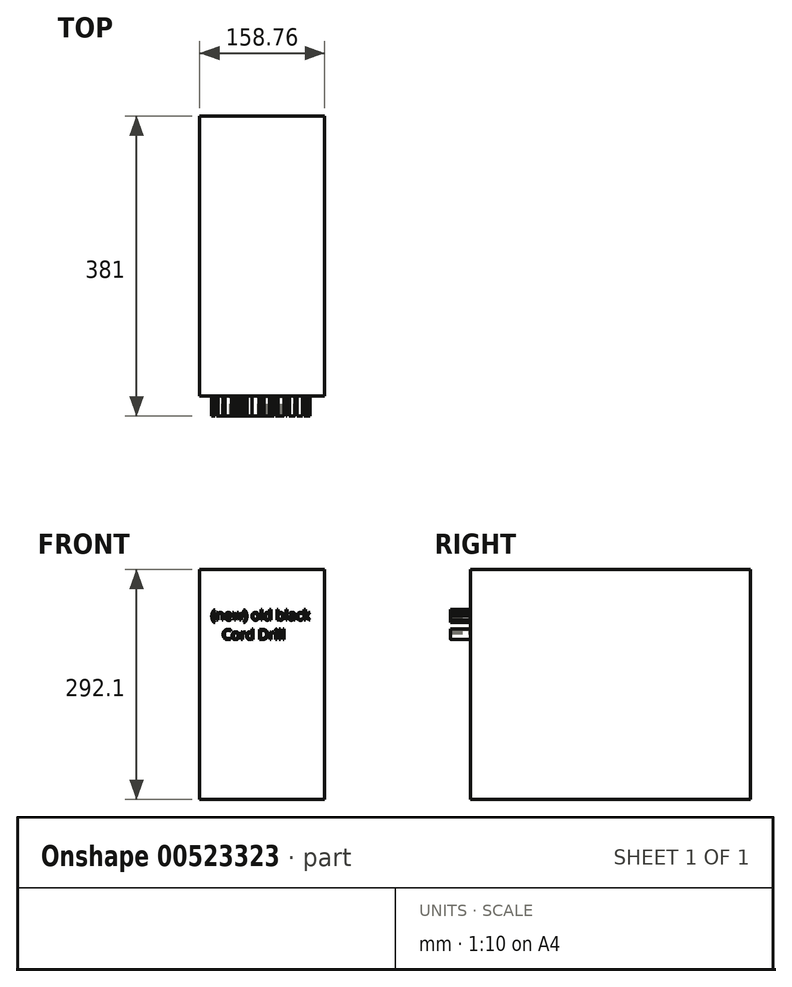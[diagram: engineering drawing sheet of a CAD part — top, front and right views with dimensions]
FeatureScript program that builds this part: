
annotation { "Feature Type Name" : "Feature", "Feature Type Description" : "" }
export const myFeature = defineFeature(function(context is Context, id is Id, definition is map)
    precondition{}
    {
        {
            var Q0;
            Q0=qCreatedBy(makeId("Front.planeOp"),FACE);
            var sketch = newSketch(context, id + "F0", { "sketchPlane" : qUnion([Q0])});
            skLineSegment(sketch, "E0.bottom", {"start": v(79.37, 146.05) * mm, "end": v(-79.38, 146.05) * mm});
            skLineSegment(sketch, "E0.top", {"start": v(79.38, -146.05) * mm, "end": v(-79.37, -146.05) * mm});
            skLineSegment(sketch, "E0.left", {"start": v(79.37, 146.05) * mm, "end": v(79.38, -146.05) * mm});
            skLineSegment(sketch, "E0.right", {"start": v(-79.38, 146.05) * mm, "end": v(-79.37, -146.05) * mm});
            skPoint(sketch, "E0.middle", {"position": v(0, 0) * mm});
            skSolve(sketch);
        }
        {
            var Q0;
            Q0=makeQuery(id+"F0.imprint","IMPRINT",FACE,{"disambiguationData":[TD([[makeQuery(id+"F0.imprint","IMPRINT",EDGE,{"derivedFrom":sQuery(id+"F0.wireOp",EDGE,"E0.bottom")}),1.0]])]});
            extrude(context, id + "F1", {"entities" : qUnion([Q0]), "depth" : 355.6 * mm, "offsetDistance" : 25.4 * mm});
        }
        {
            var Q0;
            Q0=makeQuery(id+"F1.opExtrude","CAP_FACE",FACE,{"disambiguationData":[OSD([sQuery(id+"F0.wireOp",EDGE,"E0.bottom"),sQuery(id+"F0.wireOp",EDGE,"E0.top"),sQuery(id+"F0.wireOp",EDGE,"E0.left"),sQuery(id+"F0.wireOp",EDGE,"E0.right")])],"isStart":false});
            var sketch = newSketch(context, id + "F2", { "sketchPlane" : qUnion([Q0])});
            skText(sketch, "E1", { "text": "(new) old black\n   Cord Drill", "fontName": "OpenSans-Regular.ttf"});
            const initialGuessF2  = {"E1": [-0.06474, 0.0817, 1, 0, 0.01304]};
            skSetInitialGuess(sketch, initialGuessF2);
            skSolve(sketch);
        }
        {
            var Q0;
            Q0 = qSketchRegion(id + "F2", true);
            extrude(context, id + "F3", {"entities" : qUnion([Q0]), "operationType" : NewBodyOperationType.ADD, "depth" : 25.4 * mm, "offsetDistance" : 25.4 * mm});
        }
    });
